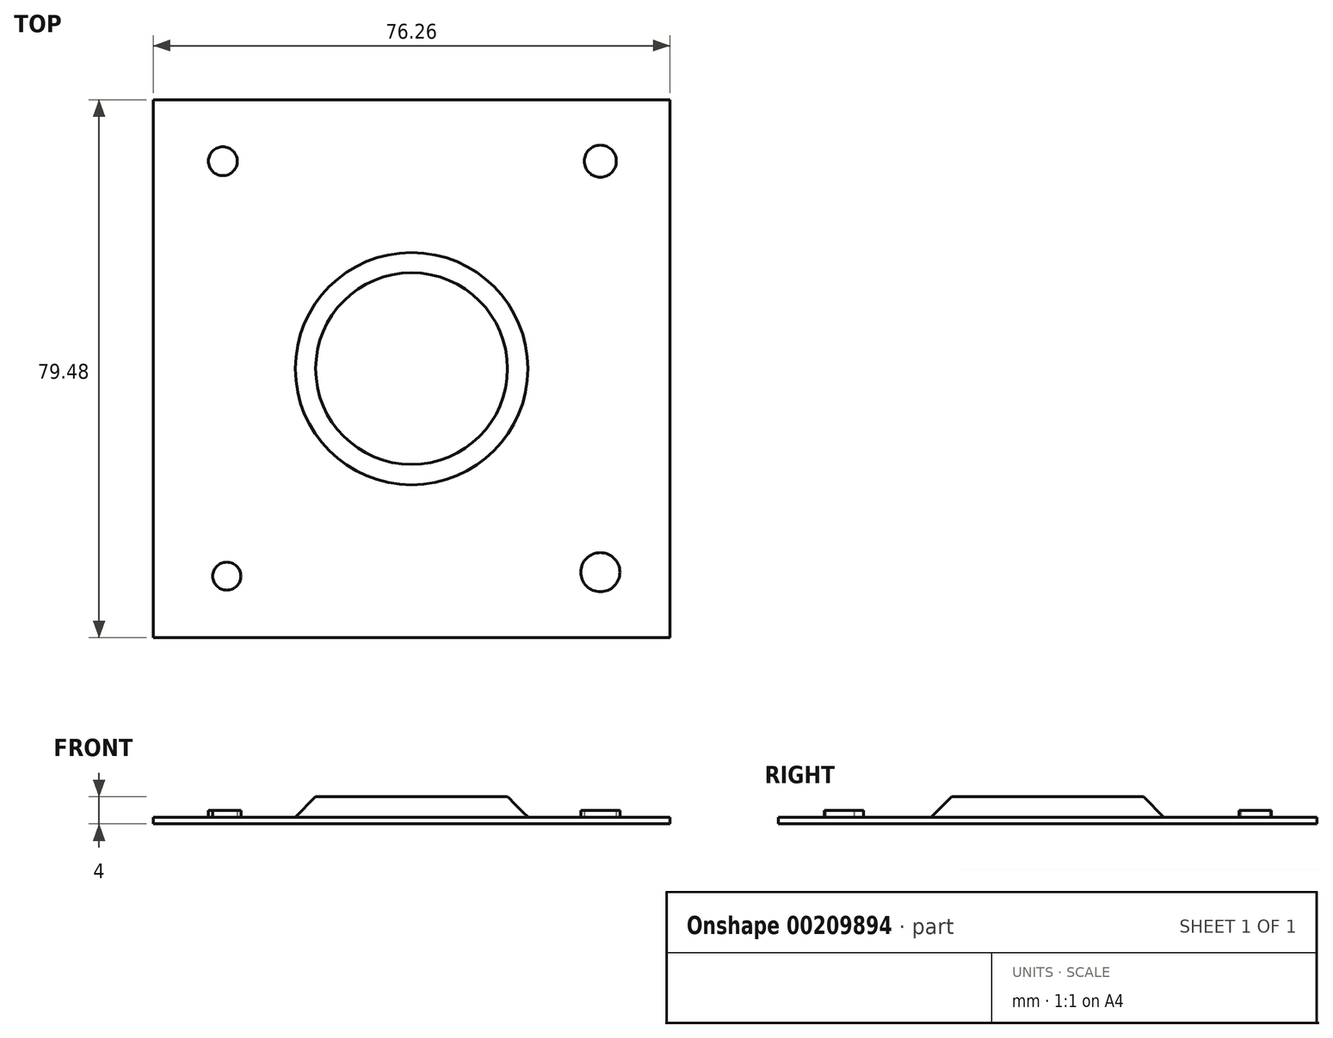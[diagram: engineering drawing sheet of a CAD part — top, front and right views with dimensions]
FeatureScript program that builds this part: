
annotation { "Feature Type Name" : "Feature", "Feature Type Description" : "" }
export const myFeature = defineFeature(function(context is Context, id is Id, definition is map)
    precondition{}
    {
        {
            var Q0;
            Q0=qCreatedBy(makeId("Top.planeOp"),FACE);
            var sketch = newSketch(context, id + "F0", { "sketchPlane" : qUnion([Q0])});
            skLineSegment(sketch, "E0.bottom", {"start": v(-38.13, 39.74) * mm, "end": v(38.13, 39.74) * mm});
            skLineSegment(sketch, "E0.top", {"start": v(-38.13, -39.74) * mm, "end": v(38.13, -39.74) * mm});
            skLineSegment(sketch, "E0.left", {"start": v(-38.13, 39.74) * mm, "end": v(-38.13, -39.74) * mm});
            skLineSegment(sketch, "E0.right", {"start": v(38.13, 39.74) * mm, "end": v(38.13, -39.74) * mm});
            skPoint(sketch, "E0.middle", {"position": v(0, 0) * mm});
            skSolve(sketch);
        }
        {
            var Q0;
            Q0=makeQuery(id+"F0.imprint","IMPRINT",FACE,{"disambiguationData":[TD([[makeQuery(id+"F0.imprint","IMPRINT",EDGE,{"derivedFrom":sQuery(id+"F0.wireOp",EDGE,"E0.bottom")}),-1.0]])]});
            var sketch = newSketch(context, id + "F1", { "sketchPlane" : qUnion([Q0])});
            skCircle(sketch, "E1", {"center": v(0, 0) * mm, "radius": 24.16 * mm});
            skSolve(sketch);
        }
        {
            var Q0;
            Q0=makeQuery(id+"F1.imprint","IMPRINT",FACE,{"disambiguationData":[TD([[makeQuery(id+"F1.imprint","IMPRINT",EDGE,{"derivedFrom":sQuery(id+"F1.wireOp",EDGE,"E1")}),1.0]])]});
            extrude(context, id + "F2", {"entities" : qUnion([Q0]), "depth" : 4 * mm});
        }
        {
            var Q0;
            Q0=makeQuery(id+"F0.imprint","IMPRINT",FACE,{"disambiguationData":[TD([[makeQuery(id+"F0.imprint","IMPRINT",EDGE,{"derivedFrom":sQuery(id+"F0.wireOp",EDGE,"E0.bottom")}),-1.0]])]});
            extrude(context, id + "F3", {"entities" : qUnion([Q0]), "operationType" : NewBodyOperationType.ADD, "depth" : 1 * mm});
        }
        {
            var Q0;
            Q0=makeQuery(id+"F3.opExtrude","CAP_FACE",FACE,{"disambiguationData":[OSD([sQuery(id+"F0.wireOp",EDGE,"E0.bottom"),sQuery(id+"F0.wireOp",EDGE,"E0.top"),sQuery(id+"F0.wireOp",EDGE,"E0.left"),sQuery(id+"F0.wireOp",EDGE,"E0.right")])],"isStart":false});
            var sketch = newSketch(context, id + "F4", { "sketchPlane" : qUnion([Q0])});
            skCircle(sketch, "E2", {"center": v(-27.28, 29.18) * mm, "radius": 2.7 * mm});
            skCircle(sketch, "E3", {"center": v(25.81, 28.89) * mm, "radius": 2.23 * mm});
            skCircle(sketch, "E4", {"center": v(25.81, -30.65) * mm, "radius": 2.07 * mm});
            skCircle(sketch, "E5", {"center": v(-27.28, -30.65) * mm, "radius": 2.07 * mm});
            skSolve(sketch);
        }
        {
            var Q0;
            Q0=makeQuery(id+"F4.imprint","IMPRINT",FACE,{"disambiguationData":[TD([[makeQuery(id+"F4.imprint","IMPRINT",EDGE,{"derivedFrom":sQuery(id+"F4.wireOp",EDGE,"E5")}),1.0]])]});
            extrude(context, id + "F5", {"entities" : qUnion([Q0]), "operationType" : NewBodyOperationType.ADD, "depth" : 1 * mm});
        }
        {
            var Q0;
            Q0=makeQuery(id+"F3.opExtrude","CAP_FACE",FACE,{"disambiguationData":[OSD([sQuery(id+"F0.wireOp",EDGE,"E0.bottom"),sQuery(id+"F0.wireOp",EDGE,"E0.top"),sQuery(id+"F0.wireOp",EDGE,"E0.left"),sQuery(id+"F0.wireOp",EDGE,"E0.right")])],"isStart":false});
            var sketch = newSketch(context, id + "F6", { "sketchPlane" : qUnion([Q0])});
            skCircle(sketch, "E6", {"center": v(-27.86, 30.65) * mm, "radius": 2.14 * mm});
            skCircle(sketch, "E7", {"center": v(27.86, 30.65) * mm, "radius": 2.36 * mm});
            skCircle(sketch, "E8", {"center": v(27.86, -30.06) * mm, "radius": 2.89 * mm});
            skSolve(sketch);
        }
        {
            var Q0;
            Q0=makeQuery(id+"F6.imprint","IMPRINT",FACE,{"disambiguationData":[TD([[makeQuery(id+"F6.imprint","IMPRINT",EDGE,{"derivedFrom":sQuery(id+"F6.wireOp",EDGE,"E8")}),1.0]])]});
            var Q1;
            Q1=makeQuery(id+"F6.imprint","IMPRINT",FACE,{"disambiguationData":[TD([[makeQuery(id+"F6.imprint","IMPRINT",EDGE,{"derivedFrom":sQuery(id+"F6.wireOp",EDGE,"E7")}),1.0]])]});
            var Q2;
            Q2=makeQuery(id+"F6.imprint","IMPRINT",FACE,{"disambiguationData":[TD([[makeQuery(id+"F6.imprint","IMPRINT",EDGE,{"derivedFrom":sQuery(id+"F6.wireOp",EDGE,"E6")}),1.0]])]});
            extrude(context, id + "F7", {"entities" : qUnion([Q0, Q1, Q2]), "operationType" : NewBodyOperationType.ADD, "depth" : 1 * mm});
        }
        {
            var Q0;
            Q0=makeQuery(id+"F2.opExtrude","CAP_EDGE",EDGE,{"disambiguationData":[OSD([sQuery(id+"F1.wireOp",EDGE,"E1")])],"isStart":false});
            chamfer(context, id + "F8", {"entities" : qUnion([Q0]), "width" : 10 * mm, "tangentPropagation" : true});
        }
    });
